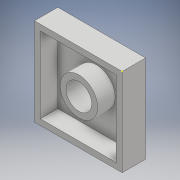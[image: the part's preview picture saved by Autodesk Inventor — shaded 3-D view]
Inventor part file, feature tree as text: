
AUTODESK INVENTOR PART (.ipt)
format: ipt  version: 2018 (Build 220112000, 112)  size: 240,128 bytes
history: native  units: mm
features: sketch x3, extrude x2, shell x1
ambient origin geometry x8: Origin, YZ Plane, XZ Plane, XY Plane, X Axis, Y Axis, Z Axis, Center Point
bodies: Solid1 (feature_tree)
feature tree (6):
  sketch  "Sketch1"  dims[d0=75.0mm d1=75.0mm]
  extrude  "Extrusion1"  Depth=75.0mm
  extrude  "Extrusion2"  Depth=5.0mm TaperAngle=0.0deg
  shell  "Shell1"  Thickness=5.0mm
  sketch  "Sketch2"  dims[d2=20.0mm d3=0.0mm d4=39.0mm d5=0.0mm d6=5.0mm]
  sketch  "Sketch3"
